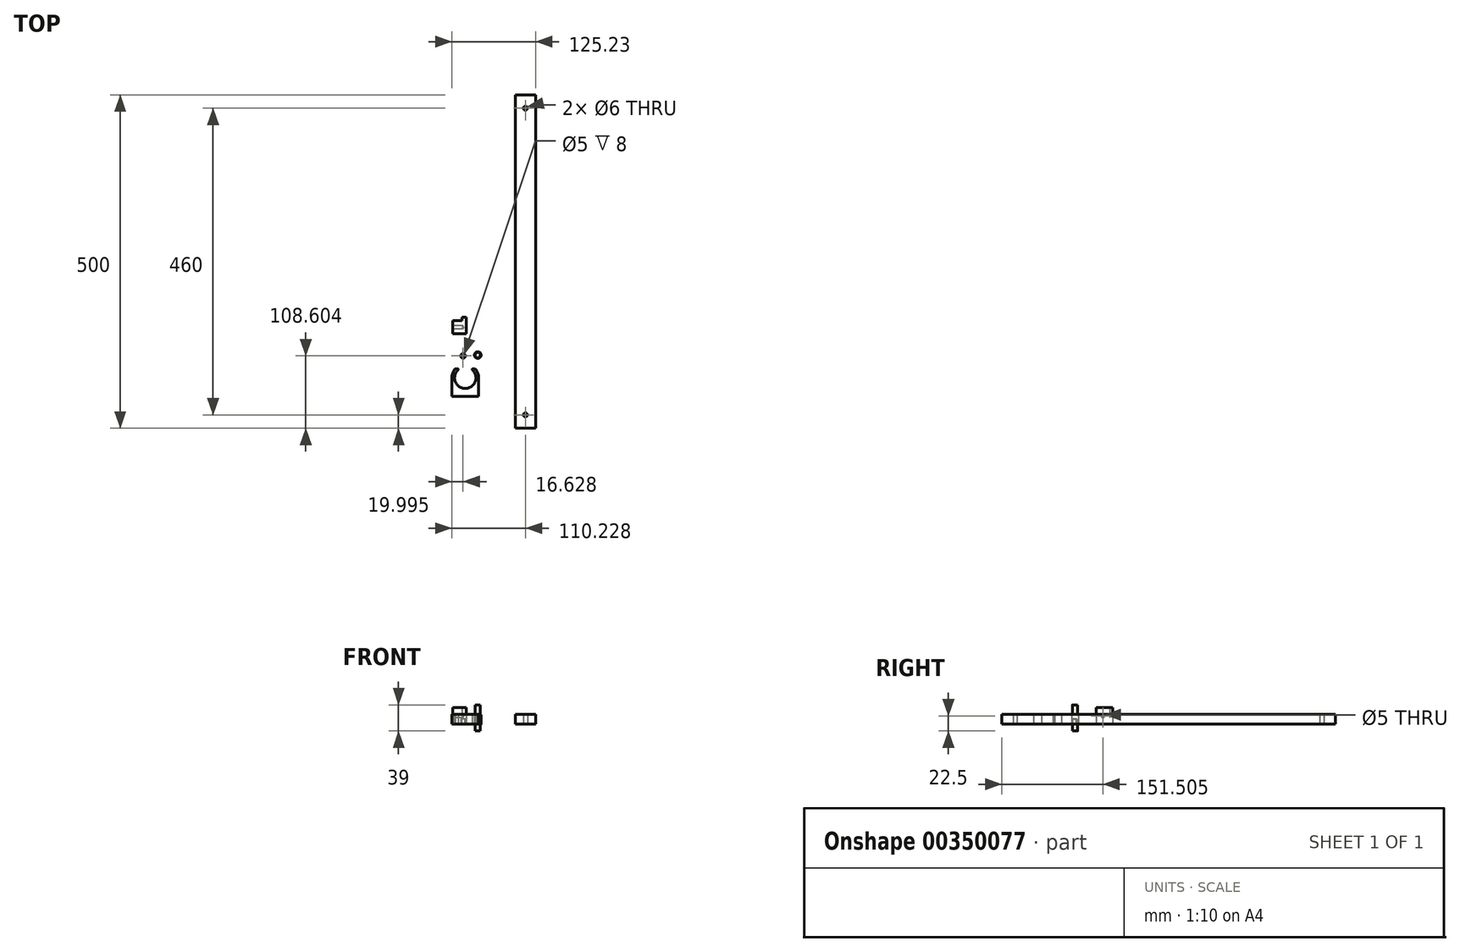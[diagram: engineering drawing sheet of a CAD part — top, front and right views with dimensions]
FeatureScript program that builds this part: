
annotation { "Feature Type Name" : "Feature", "Feature Type Description" : "" }
export const myFeature = defineFeature(function(context is Context, id is Id, definition is map)
    precondition{}
    {
        {
            var Q0;
            Q0=qCreatedBy(makeId("Top.planeOp"),FACE);
            var sketch = newSketch(context, id + "F0", { "sketchPlane" : qUnion([Q0])});
            skCircle(sketch, "E0", {"center": v(-30.93, 12) * mm, "radius": 2.5 * mm});
            skCircle(sketch, "E1", {"center": v(-30.93, 12) * mm, "radius": 3.5 * mm});
            skCircle(sketch, "E2", {"center": v(-8.9, 13.1) * mm, "radius": 4 * mm});
            skCircle(sketch, "E3", {"center": v(-8.9, 13.1) * mm, "radius": 5 * mm});
            skLineSegment(sketch, "E4.bottom", {"start": v(47.67, 403.39) * mm, "end": v(77.67, 403.39) * mm});
            skLineSegment(sketch, "E4.top", {"start": v(47.67, -96.61) * mm, "end": v(77.67, -96.61) * mm});
            skLineSegment(sketch, "E4.left", {"start": v(47.67, 403.39) * mm, "end": v(47.67, -96.61) * mm});
            skLineSegment(sketch, "E4.right", {"start": v(77.67, 403.39) * mm, "end": v(77.67, -96.61) * mm});
            skPoint(sketch, "E5", {"position": v(62.67, 383.39) * mm});
            skPoint(sketch, "E5.positionSnap0", {"position": v(62.67, 403.39) * mm});
            skPoint(sketch, "E6", {"position": v(62.67, -76.61) * mm});
            skPoint(sketch, "E6.positionSnap0", {"position": v(62.67, -96.61) * mm});
            skLineSegment(sketch, "E7", {"start": v(47.67, 153.39) * mm, "end": v(77.67, 153.39) * mm, "construction": true});
            skLineSegment(sketch, "E8", {"start": v(-46.17, 44.9) * mm, "end": v(-26.17, 44.9) * mm});
            skLineSegment(sketch, "E9", {"start": v(-26.17, 44.9) * mm, "end": v(-26.17, 69.9) * mm});
            skLineSegment(sketch, "E10", {"start": v(-26.17, 69.9) * mm, "end": v(-32.17, 69.9) * mm});
            skLineSegment(sketch, "E11", {"start": v(-32.17, 69.9) * mm, "end": v(-32.17, 64.9) * mm});
            skLineSegment(sketch, "E12", {"start": v(-32.17, 64.9) * mm, "end": v(-46.17, 64.9) * mm});
            skLineSegment(sketch, "E13", {"start": v(-46.17, 64.9) * mm, "end": v(-46.17, 44.9) * mm});
            skArc(sketch, "E14", {"start": v(-38.34, -9.06) * mm, "mid": v(-27.65, -36.97) * mm, "end": v(-16.96, -9.06) * mm});
            skLineSegment(sketch, "E15.left", {"start": v(-7.56, -45.1) * mm, "end": v(-7.48, -19.98) * mm});
            skLineSegment(sketch, "E15.right", {"start": v(-47.56, -42.2) * mm, "end": v(-47.48, -17.2) * mm});
            skLineSegment(sketch, "E16", {"start": v(-47.56, -42.2) * mm, "end": v(-47.56, -48.97) * mm});
            skLineSegment(sketch, "E17", {"start": v(-47.56, -48.97) * mm, "end": v(-7.56, -48.97) * mm});
            skLineSegment(sketch, "E18", {"start": v(-7.56, -48.97) * mm, "end": v(-7.56, -45.1) * mm});
            skArc(sketch, "E19", {"start": v(-7.48, -19.98) * mm, "mid": v(-9.02, -13.18) * mm, "end": v(-12.77, -7.32) * mm});
            skLineSegment(sketch, "E20", {"start": v(-42.52, -7.32) * mm, "end": v(-39, -7.32) * mm});
            skArc(sketch, "E21.trimOffspring", {"start": v(-42.52, -7.32) * mm, "mid": v(-45.7, -11.91) * mm, "end": v(-47.48, -17.2) * mm});
            skLineSegment(sketch, "E22.trimOffspring", {"start": v(-16.29, -7.32) * mm, "end": v(-12.77, -7.32) * mm});
            skPoint(sketch, "E23.visualSharp", {"position": v(-36, -7.32) * mm});
            skArc(sketch, "E23.filletArc", {"start": v(-38.34, -9.06) * mm, "mid": v(-38.07, -7.96) * mm, "end": v(-39, -7.32) * mm});
            skPoint(sketch, "E24.visualSharp", {"position": v(-19.3, -7.32) * mm});
            skArc(sketch, "E24.filletArc", {"start": v(-16.29, -7.32) * mm, "mid": v(-17.22, -7.96) * mm, "end": v(-16.96, -9.06) * mm});
            skSolve(sketch);
        }
        {
            var Q0;
            Q0=makeQuery(id+"F0.imprint","IMPRINT",FACE,{"disambiguationData":[TD([[makeQuery(id+"F0.imprint","IMPRINT",EDGE,{"derivedFrom":sQuery(id+"F0.wireOp",EDGE,"E0")}),-1.0]])]});
            extrude(context, id + "F1", {"entities" : qUnion([Q0]), "depth" : 8 * mm});
        }
        {
            var Q0;
            Q0=makeQuery(id+"F0.imprint","IMPRINT",FACE,{"disambiguationData":[TD([[makeQuery(id+"F0.imprint","IMPRINT",EDGE,{"derivedFrom":sQuery(id+"F0.wireOp",EDGE,"E2")}),1.0]])]});
            extrude(context, id + "F2", {"entities" : qUnion([Q0]), "oppositeDirection" : true, "depth" : 10 * mm});
        }
        {
            var Q0;
            Q0=makeQuery(id+"F0.imprint","IMPRINT",FACE,{"disambiguationData":[TD([[makeQuery(id+"F0.imprint","IMPRINT",EDGE,{"derivedFrom":sQuery(id+"F0.wireOp",EDGE,"E2")}),-1.0]])]});
            var Q1;
            Q1=makeQuery(id+"F0.imprint","IMPRINT",FACE,{"disambiguationData":[TD([[makeQuery(id+"F0.imprint","IMPRINT",EDGE,{"derivedFrom":sQuery(id+"F0.wireOp",EDGE,"E2")}),1.0]])]});
            extrude(context, id + "F3", {"entities" : qUnion([Q0, Q1]), "operationType" : NewBodyOperationType.ADD, "depth" : 14 * mm});
        }
        {
            var Q0;
            Q0=makeQuery(id+"F3.opExtrude","CAP_FACE",FACE,{"disambiguationData":[OSD([sQuery(id+"F0.wireOp",EDGE,"E3")])],"isStart":false});
            var sketch = newSketch(context, id + "F4", { "sketchPlane" : qUnion([Q0])});
            skCircle(sketch, "E25.0", {"center": v(-8.9, 13.1) * mm, "radius": 4 * mm});
            skSolve(sketch);
        }
        {
            var Q0;
            Q0=makeQuery(id+"F4.imprint","IMPRINT",FACE,{"disambiguationData":[TD([[makeQuery(id+"F4.imprint","IMPRINT",EDGE,{"derivedFrom":sQuery(id+"F4.wireOp",EDGE,"E25.0")}),1.0]])]});
            extrude(context, id + "F5", {"entities" : qUnion([Q0]), "operationType" : NewBodyOperationType.ADD, "depth" : 15 * mm});
        }
        {
            var Q0;
            Q0=makeQuery(id+"F0.imprint","IMPRINT",FACE,{"disambiguationData":[TD([[makeQuery(id+"F0.imprint","IMPRINT",EDGE,{"derivedFrom":sQuery(id+"F0.wireOp",EDGE,"E4.bottom")}),-1.0]])]});
            extrude(context, id + "F6", {"entities" : qUnion([Q0]), "depth" : 15 * mm});
        }
        {
            var Q0;
            Q0=sQuery(id+"F0.wireOp",VERTEX,"E5");
            var Q1;
            Q1=sQuery(id+"F0.wireOp",VERTEX,"E6");
            var Q2;
            Q2=makeQuery(id+"F6.opExtrude","SWEPT_BODY",BODY,{"disambiguationData":[OSD([sQuery(id+"F0.wireOp",EDGE,"E4.bottom"),sQuery(id+"F0.wireOp",EDGE,"E4.top"),sQuery(id+"F0.wireOp",EDGE,"E4.left"),sQuery(id+"F0.wireOp",EDGE,"E4.right")])]});
            hole(context, id + "F7", {"style" : HoleStyle.SIMPLE, "endStyle" : HoleEndStyle.THROUGH, "oppositeDirection" : true, "holeDiameter" : 6 * mm, "isTappedThrough" : true, "tappedDepth" : 12 * mm, "tapClearance" : 3, "locations" : qUnion([Q0, Q1]), "scope" : qUnion([Q2])});
        }
        {
            var Q0;
            Q0=makeQuery(id+"F0.imprint","IMPRINT",FACE,{"disambiguationData":[TD([[makeQuery(id+"F0.imprint","IMPRINT",EDGE,{"derivedFrom":sQuery(id+"F0.wireOp",EDGE,"E8")}),1.0]])]});
            extrude(context, id + "F8", {"entities" : qUnion([Q0]), "depth" : 25 * mm});
        }
        {
            var Q0;
            Q0=makeQuery(id+"F8.opExtrude","SWEPT_FACE",FACE,{"disambiguationData":[OSD([sQuery(id+"F0.wireOp",EDGE,"E13")])]});
            var sketch = newSketch(context, id + "F9", { "sketchPlane" : qUnion([Q0])});
            skLineSegment(sketch, "E26", {"start": v(-54.9, 25) * mm, "end": v(-54.9, 0) * mm, "construction": true});
            skLineSegment(sketch, "E27", {"start": v(-64.9, 12.5) * mm, "end": v(-44.9, 12.5) * mm, "construction": true});
            skPoint(sketch, "E28", {"position": v(-54.9, 12.5) * mm});
            skSolve(sketch);
        }
        {
            var Q0;
            Q0=sQuery(id+"F9.wireOp",VERTEX,"E28");
            var Q1;
            Q1=makeQuery(id+"F6.opExtrude","SWEPT_BODY",BODY,{"disambiguationData":[OSD([sQuery(id+"F0.wireOp",EDGE,"E4.bottom"),sQuery(id+"F0.wireOp",EDGE,"E4.top"),sQuery(id+"F0.wireOp",EDGE,"E4.left"),sQuery(id+"F0.wireOp",EDGE,"E4.right")])]});
            var Q2;
            Q2=makeQuery(id+"F8.opExtrude","SWEPT_BODY",BODY,{"disambiguationData":[OSD([sQuery(id+"F0.wireOp",EDGE,"E8"),sQuery(id+"F0.wireOp",EDGE,"E9"),sQuery(id+"F0.wireOp",EDGE,"E10"),sQuery(id+"F0.wireOp",EDGE,"E11"),sQuery(id+"F0.wireOp",EDGE,"E12"),sQuery(id+"F0.wireOp",EDGE,"E13")])]});
            hole(context, id + "F10", {"style" : HoleStyle.SIMPLE, "endStyle" : HoleEndStyle.BLIND, "holeDiameter" : 5 * mm, "holeDepth" : 15 * mm, "isTappedThrough" : true, "tappedDepth" : 12 * mm, "tapClearance" : 3, "locations" : qUnion([Q0]), "scope" : qUnion([Q1, Q2])});
        }
        {
            var Q0;
            Q0=makeQuery(id+"F0.imprint","IMPRINT",FACE,{"disambiguationData":[TD([[makeQuery(id+"F0.imprint","IMPRINT",EDGE,{"derivedFrom":sQuery(id+"F0.wireOp",EDGE,"E14")}),-1.0]])]});
            extrude(context, id + "F11", {"entities" : qUnion([Q0]), "depth" : 15 * mm});
        }
    });
